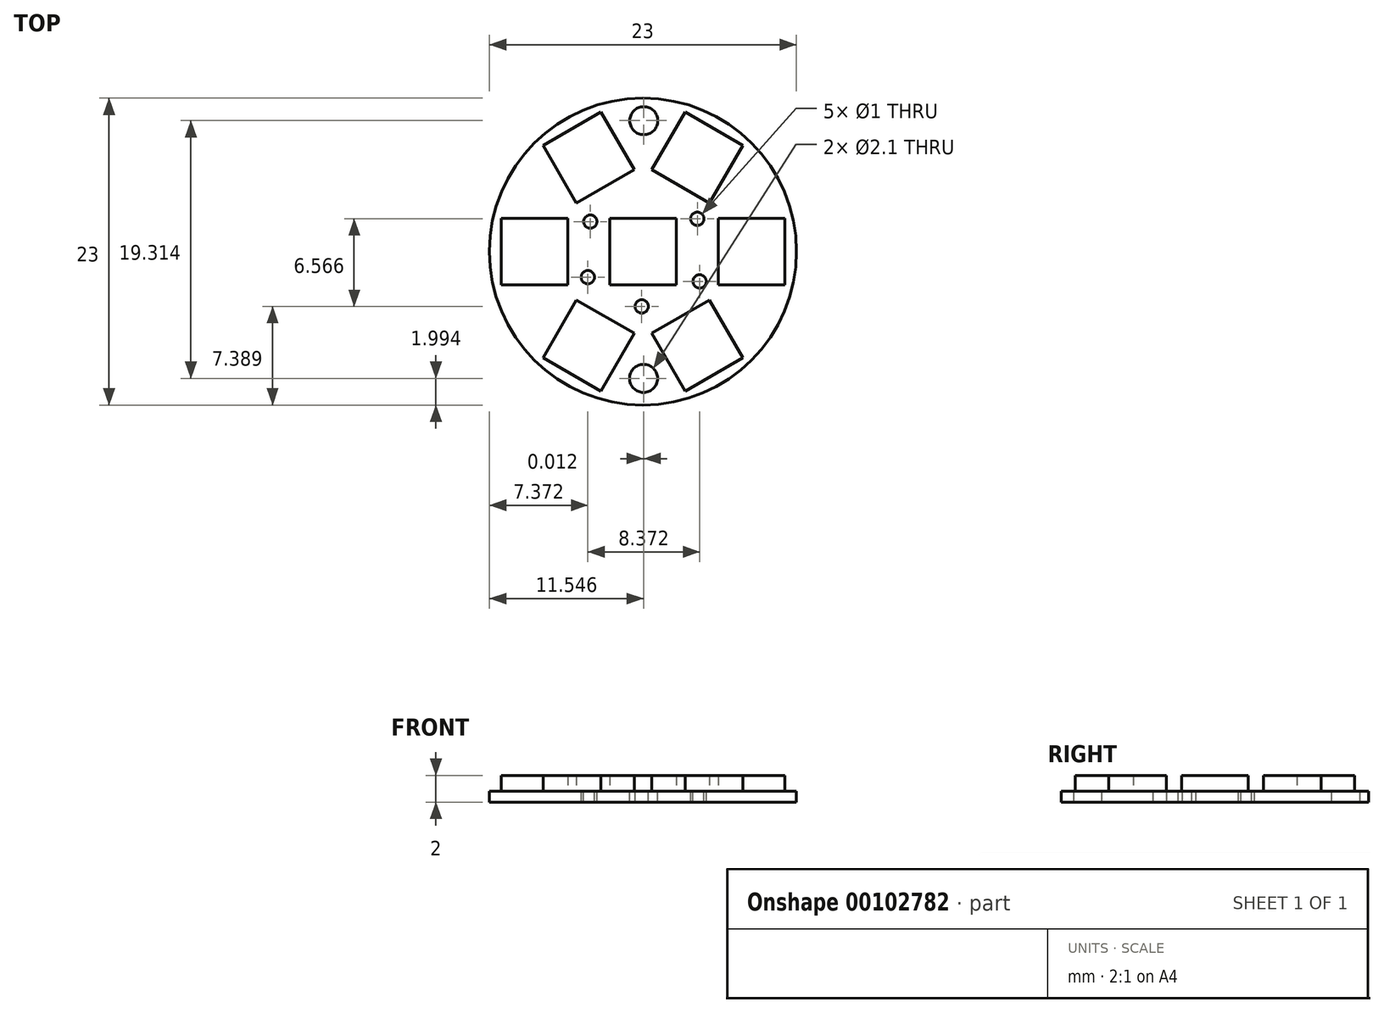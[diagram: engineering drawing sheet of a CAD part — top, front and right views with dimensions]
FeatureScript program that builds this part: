
annotation { "Feature Type Name" : "Feature", "Feature Type Description" : "" }
export const myFeature = defineFeature(function(context is Context, id is Id, definition is map)
    precondition{}
    {
        {
            var Q0;
            Q0=qCreatedBy(makeId("Top.planeOp"),FACE);
            var sketch = newSketch(context, id + "F0", { "sketchPlane" : qUnion([Q0])});
            skCircle(sketch, "E0", {"center": v(0, 0) * mm, "radius": 11.5 * mm});
            skLineSegment(sketch, "E1", {"start": v(-11.5, 11.5) * mm, "end": v(11.5, -11.5) * mm, "construction": true});
            skLineSegment(sketch, "E2.rect.bottom", {"start": v(2.5, 2.5) * mm, "end": v(-2.5, 2.5) * mm});
            skLineSegment(sketch, "E2.rect.top", {"start": v(2.5, -2.5) * mm, "end": v(-2.5, -2.5) * mm});
            skLineSegment(sketch, "E2.rect.left", {"start": v(2.5, 2.5) * mm, "end": v(2.5, -2.5) * mm});
            skLineSegment(sketch, "E2.rect.right", {"start": v(-2.5, 2.5) * mm, "end": v(-2.5, -2.5) * mm});
            skLineSegment(sketch, "E3", {"start": v(0, 0) * mm, "end": v(14.29, 0) * mm, "construction": true});
            skLineSegment(sketch, "E4.rect.bottom", {"start": v(5.63, 2.5) * mm, "end": v(10.63, 2.5) * mm});
            skLineSegment(sketch, "E4.rect.top", {"start": v(5.63, -2.5) * mm, "end": v(10.63, -2.5) * mm});
            skLineSegment(sketch, "E4.rect.left", {"start": v(5.63, 2.5) * mm, "end": v(5.63, -2.5) * mm});
            skLineSegment(sketch, "E4.rect.right", {"start": v(10.63, 2.5) * mm, "end": v(10.63, -2.5) * mm});
            skPoint(sketch, "E4.rect.middle", {"position": v(8.13, 0) * mm});
            skLineSegment(sketch, "E5.1.0", {"start": v(0.65, 6.13) * mm, "end": v(3.15, 10.46) * mm});
            skLineSegment(sketch, "E5.1.1", {"start": v(3.15, 10.46) * mm, "end": v(7.48, 7.96) * mm});
            skLineSegment(sketch, "E5.1.2", {"start": v(4.98, 3.63) * mm, "end": v(7.48, 7.96) * mm});
            skLineSegment(sketch, "E5.1.3", {"start": v(0.65, 6.13) * mm, "end": v(4.98, 3.63) * mm});
            skLineSegment(sketch, "E5.2.0", {"start": v(-4.98, 3.63) * mm, "end": v(-7.48, 7.96) * mm});
            skLineSegment(sketch, "E5.2.1", {"start": v(-7.48, 7.96) * mm, "end": v(-3.15, 10.46) * mm});
            skLineSegment(sketch, "E5.2.2", {"start": v(-0.65, 6.13) * mm, "end": v(-3.15, 10.46) * mm});
            skLineSegment(sketch, "E5.2.3", {"start": v(-4.98, 3.63) * mm, "end": v(-0.65, 6.13) * mm});
            skLineSegment(sketch, "E5.3.0", {"start": v(-5.63, -2.5) * mm, "end": v(-10.63, -2.5) * mm});
            skLineSegment(sketch, "E5.3.1", {"start": v(-10.63, -2.5) * mm, "end": v(-10.63, 2.5) * mm});
            skLineSegment(sketch, "E5.3.2", {"start": v(-5.63, 2.5) * mm, "end": v(-10.63, 2.5) * mm});
            skLineSegment(sketch, "E5.3.3", {"start": v(-5.63, -2.5) * mm, "end": v(-5.63, 2.5) * mm});
            skLineSegment(sketch, "E5.4.0", {"start": v(-0.65, -6.13) * mm, "end": v(-3.15, -10.46) * mm});
            skLineSegment(sketch, "E5.4.1", {"start": v(-3.15, -10.46) * mm, "end": v(-7.48, -7.96) * mm});
            skLineSegment(sketch, "E5.4.2", {"start": v(-4.98, -3.63) * mm, "end": v(-7.48, -7.96) * mm});
            skLineSegment(sketch, "E5.4.3", {"start": v(-0.65, -6.13) * mm, "end": v(-4.98, -3.63) * mm});
            skLineSegment(sketch, "E6.1.5.0", {"start": v(4.98, -3.63) * mm, "end": v(7.48, -7.96) * mm});
            skLineSegment(sketch, "E6.3.5.0", {"start": v(7.48, -7.96) * mm, "end": v(3.15, -10.46) * mm});
            skLineSegment(sketch, "E6.6.5.0", {"start": v(0.65, -6.13) * mm, "end": v(3.15, -10.46) * mm});
            skLineSegment(sketch, "E6.9.5.0", {"start": v(4.98, -3.63) * mm, "end": v(0.65, -6.13) * mm});
            skCircle(sketch, "E7", {"center": v(-3.95, 2.25) * mm, "radius": 0.5 * mm});
            skCircle(sketch, "E8", {"center": v(4.24, -2.24) * mm, "radius": 0.5 * mm});
            skCircle(sketch, "E9", {"center": v(4.07, 2.46) * mm, "radius": 0.5 * mm});
            skCircle(sketch, "E10", {"center": v(-0.1, -4.11) * mm, "radius": 0.5 * mm});
            skCircle(sketch, "E11", {"center": v(-4.13, -1.92) * mm, "radius": 0.5 * mm});
            skCircle(sketch, "E12", {"center": v(0.06, 9.8) * mm, "radius": 1.05 * mm});
            skCircle(sketch, "E13", {"center": v(0.05, -9.5) * mm, "radius": 1.05 * mm});
            skSolve(sketch);
        }
        {
            var Q0;
            Q0=makeQuery(id+"F0.imprint","IMPRINT",FACE,{"disambiguationData":[TD([[makeQuery(id+"F0.imprint","IMPRINT",EDGE,{"derivedFrom":sQuery(id+"F0.wireOp",EDGE,"E0")}),1.0]])]});
            var Q1;
            Q1=makeQuery(id+"F0.imprint","IMPRINT",FACE,{"disambiguationData":[TD([[makeQuery(id+"F0.imprint","IMPRINT",EDGE,{"derivedFrom":sQuery(id+"F0.wireOp",EDGE,"E5.2.0")}),-1.0]])]});
            var Q2;
            Q2=makeQuery(id+"F0.imprint","IMPRINT",FACE,{"disambiguationData":[TD([[makeQuery(id+"F0.imprint","IMPRINT",EDGE,{"derivedFrom":sQuery(id+"F0.wireOp",EDGE,"E5.1.0")}),-1.0]])]});
            var Q3;
            Q3=makeQuery(id+"F0.imprint","IMPRINT",FACE,{"disambiguationData":[TD([[makeQuery(id+"F0.imprint","IMPRINT",EDGE,{"derivedFrom":sQuery(id+"F0.wireOp",EDGE,"E4.rect.bottom")}),-1.0]])]});
            var Q4;
            Q4=makeQuery(id+"F0.imprint","IMPRINT",FACE,{"disambiguationData":[TD([[makeQuery(id+"F0.imprint","IMPRINT",EDGE,{"derivedFrom":sQuery(id+"F0.wireOp",EDGE,"E5.3.0")}),-1.0]])]});
            var Q5;
            Q5=makeQuery(id+"F0.imprint","IMPRINT",FACE,{"disambiguationData":[TD([[makeQuery(id+"F0.imprint","IMPRINT",EDGE,{"derivedFrom":sQuery(id+"F0.wireOp",EDGE,"E2.rect.bottom")}),1.0]])]});
            var Q6;
            Q6=makeQuery(id+"F0.imprint","IMPRINT",FACE,{"disambiguationData":[TD([[makeQuery(id+"F0.imprint","IMPRINT",EDGE,{"derivedFrom":sQuery(id+"F0.wireOp",EDGE,"E5.4.0")}),-1.0]])]});
            var Q7;
            Q7=makeQuery(id+"F0.imprint","IMPRINT",FACE,{"disambiguationData":[TD([[makeQuery(id+"F0.imprint","IMPRINT",EDGE,{"derivedFrom":sQuery(id+"F0.wireOp",EDGE,"E6.1.5.0")}),-1.0]])]});
            extrude(context, id + "F1", {"entities" : qUnion([Q0, Q1, Q2, Q3, Q4, Q5, Q6, Q7]), "oppositeDirection" : true, "depth" : .8 * mm});
        }
        {
            var Q0;
            Q0=makeQuery(id+"F0.imprint","IMPRINT",FACE,{"disambiguationData":[TD([[makeQuery(id+"F0.imprint","IMPRINT",EDGE,{"derivedFrom":sQuery(id+"F0.wireOp",EDGE,"E5.2.0")}),-1.0]])]});
            var Q1;
            Q1=makeQuery(id+"F0.imprint","IMPRINT",FACE,{"disambiguationData":[TD([[makeQuery(id+"F0.imprint","IMPRINT",EDGE,{"derivedFrom":sQuery(id+"F0.wireOp",EDGE,"E5.1.0")}),-1.0]])]});
            var Q2;
            Q2=makeQuery(id+"F0.imprint","IMPRINT",FACE,{"disambiguationData":[TD([[makeQuery(id+"F0.imprint","IMPRINT",EDGE,{"derivedFrom":sQuery(id+"F0.wireOp",EDGE,"E5.3.0")}),-1.0]])]});
            var Q3;
            Q3=makeQuery(id+"F0.imprint","IMPRINT",FACE,{"disambiguationData":[TD([[makeQuery(id+"F0.imprint","IMPRINT",EDGE,{"derivedFrom":sQuery(id+"F0.wireOp",EDGE,"E2.rect.bottom")}),1.0]])]});
            var Q4;
            Q4=makeQuery(id+"F0.imprint","IMPRINT",FACE,{"disambiguationData":[TD([[makeQuery(id+"F0.imprint","IMPRINT",EDGE,{"derivedFrom":sQuery(id+"F0.wireOp",EDGE,"E4.rect.bottom")}),-1.0]])]});
            var Q5;
            Q5=makeQuery(id+"F0.imprint","IMPRINT",FACE,{"disambiguationData":[TD([[makeQuery(id+"F0.imprint","IMPRINT",EDGE,{"derivedFrom":sQuery(id+"F0.wireOp",EDGE,"E5.4.0")}),-1.0]])]});
            var Q6;
            Q6=makeQuery(id+"F0.imprint","IMPRINT",FACE,{"disambiguationData":[TD([[makeQuery(id+"F0.imprint","IMPRINT",EDGE,{"derivedFrom":sQuery(id+"F0.wireOp",EDGE,"E6.1.5.0")}),-1.0]])]});
            extrude(context, id + "F2", {"entities" : qUnion([Q0, Q1, Q2, Q3, Q4, Q5, Q6]), "operationType" : NewBodyOperationType.ADD, "depth" : 1.2 * mm});
        }
    });
